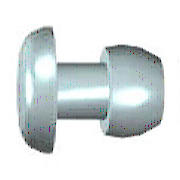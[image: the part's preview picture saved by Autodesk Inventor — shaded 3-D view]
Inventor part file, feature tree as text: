
AUTODESK INVENTOR PART (.ipt)
format: ipt  version: 2023.2 (Build 272271030, 271C)  size: 164,352 bytes
history: native  units: mm
features: revolve x1, sketch x1
ambient origin geometry x8: Origin, YZ Plane, XZ Plane, XY Plane, X Axis, Y Axis, Z Axis, Center Point
bodies: Body1 (feature_tree)
feature tree (2):
  revolve  "Revolution 1"  [1 undecoded]
  sketch  "Sketch1"  dims[d16=90.0deg d21=2.0mm d22=5.555mm d23=7.272mm d27=6.0mm d28=10.1mm]
note: 1 required parameter value undecoded (feature->parameter linkage not recoverable at this tier; creation-order binding heuristic only, values carry confidence <= 0.55)
